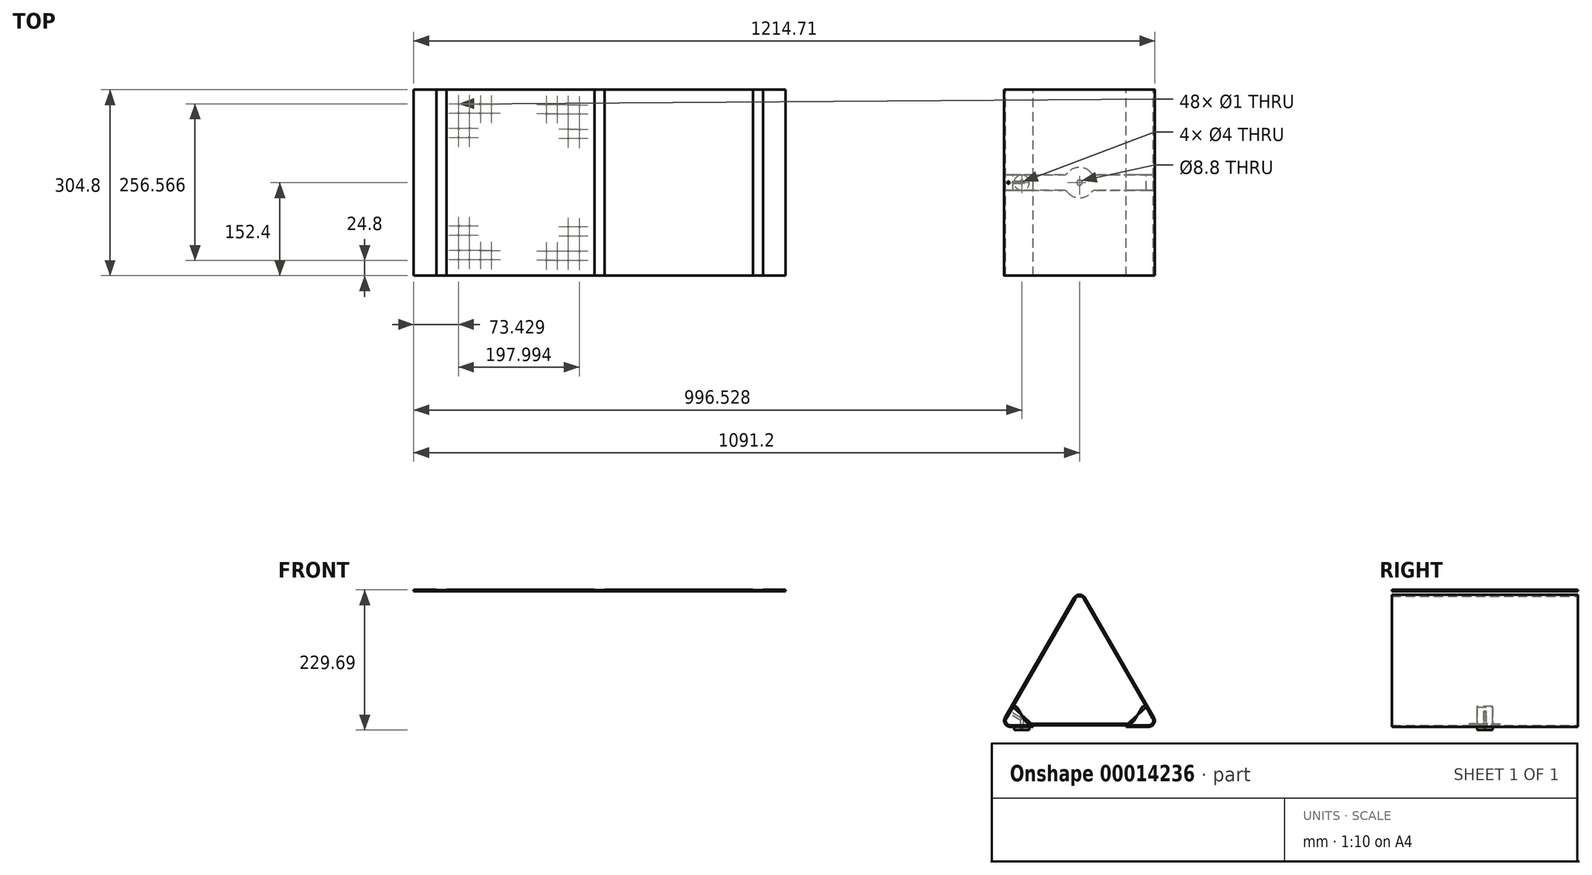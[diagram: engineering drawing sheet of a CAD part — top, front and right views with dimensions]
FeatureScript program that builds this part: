
annotation { "Feature Type Name" : "Feature", "Feature Type Description" : "" }
export const myFeature = defineFeature(function(context is Context, id is Id, definition is map)
    precondition{}
    {
        {
            var Q0;
            Q0=qCreatedBy(makeId("Front.planeOp"),FACE);
            var sketch = newSketch(context, id + "F0", { "sketchPlane" : qUnion([Q0])});
            skLineSegment(sketch, "E0", {"start": v(-6.93, -12) * mm, "end": v(-120.07, -207.97) * mm});
            skLineSegment(sketch, "E1", {"start": v(-113.14, -219.97) * mm, "end": v(-76.2, -219.97) * mm});
            skLineSegment(sketch, "E2", {"start": v(0, 0) * mm, "end": v(0, -169.94) * mm, "construction": true});
            skLineSegment(sketch, "E3.MirrorCS", {"start": v(6.93, -12) * mm, "end": v(120.07, -207.97) * mm});
            skLineSegment(sketch, "E4.MirrorCS", {"start": v(113.14, -219.97) * mm, "end": v(76.2, -219.97) * mm});
            skPoint(sketch, "E5.visualSharp", {"position": v(0, 0) * mm});
            skArc(sketch, "E5.filletArc", {"start": v(6.93, -12) * mm, "mid": v(0, -8) * mm, "end": v(-6.93, -12) * mm});
            skPoint(sketch, "E6.visualSharp", {"position": v(127, -219.97) * mm});
            skArc(sketch, "E6.filletArc", {"start": v(113.14, -219.97) * mm, "mid": v(120.07, -215.97) * mm, "end": v(120.07, -207.97) * mm});
            skPoint(sketch, "E7.visualSharp", {"position": v(-127, -219.97) * mm});
            skArc(sketch, "E7.filletArc", {"start": v(-120.07, -207.97) * mm, "mid": v(-120.07, -215.97) * mm, "end": v(-113.14, -219.97) * mm});
            skLineSegment(sketch, "E8.0", {"start": v(113.14, -222.33) * mm, "end": v(76.2, -222.33) * mm});
            skArc(sketch, "E8.1", {"start": v(113.14, -222.33) * mm, "mid": v(122.12, -217.15) * mm, "end": v(122.12, -206.79) * mm});
            skLineSegment(sketch, "E8.2", {"start": v(8.97, -10.82) * mm, "end": v(122.12, -206.79) * mm});
            skLineSegment(sketch, "E8.3", {"start": v(-113.14, -222.33) * mm, "end": v(-76.2, -222.33) * mm});
            skArc(sketch, "E8.4", {"start": v(-122.12, -206.79) * mm, "mid": v(-122.12, -217.15) * mm, "end": v(-113.14, -222.33) * mm});
            skLineSegment(sketch, "E8.5", {"start": v(-8.97, -10.82) * mm, "end": v(-122.12, -206.79) * mm});
            skArc(sketch, "E8.6", {"start": v(8.97, -10.82) * mm, "mid": v(0, -5.64) * mm, "end": v(-8.97, -10.82) * mm});
            skLineSegment(sketch, "E9", {"start": v(-76.2, -219.97) * mm, "end": v(-76.2, -222.33) * mm});
            skLineSegment(sketch, "E10", {"start": v(76.2, -219.97) * mm, "end": v(76.2, -222.33) * mm});
            skSolve(sketch);
        }
        {
            var Q0;
            Q0 = qSketchRegion(id + "F0", true);
            extrude(context, id + "F1", {"entities" : qUnion([Q0]), "depth" : 304.8 * mm});
        }
        {
            var Q0;
            Q0=qCreatedBy(makeId("Front.planeOp"),FACE);
            cPlane(context, id + "F2", {"entities" : qUnion([Q0]), "cplaneType" : CPlaneType.OFFSET, "offset" : 152.4 * mm, "width" : 150 * mm, "height" : 150 * mm});
        }
        {
            var Q0;
            Q0=qCreatedBy(id+"F2.planeOp",FACE);
            var sketch = newSketch(context, id + "F3", { "sketchPlane" : qUnion([Q0])});
            skLineSegment(sketch, "E11.0", {"start": v(-106, -183.58) * mm, "end": v(-120.07, -207.97) * mm});
            skArc(sketch, "E12.0", {"start": v(-120.07, -207.97) * mm, "mid": v(-120.07, -215.97) * mm, "end": v(-113.14, -219.97) * mm});
            skPoint(sketch, "E13.orphan", {"position": v(-6.93, -12) * mm});
            skPoint(sketch, "E14.orphan", {"position": v(6.93, -12) * mm});
            skLineSegment(sketch, "E15.0", {"start": v(0, -216.97) * mm, "end": v(-86.71, -216.97) * mm});
            skLineSegment(sketch, "E16", {"start": v(-106, -183.58) * mm, "end": v(-86.71, -216.97) * mm});
            skLineSegment(sketch, "E17", {"start": v(0, -219.97) * mm, "end": v(0, -162.05) * mm, "construction": true});
            skLineSegment(sketch, "E18.trimOffspring", {"start": v(0, -219.97) * mm, "end": v(-113.14, -219.97) * mm});
            skPoint(sketch, "E19.0.start.orphan", {"position": v(113.14, -219.97) * mm});
            skLineSegment(sketch, "E20.MirrorCS", {"start": v(0, -216.97) * mm, "end": v(86.71, -216.97) * mm});
            skLineSegment(sketch, "E21.MirrorCS", {"start": v(0, -219.97) * mm, "end": v(113.14, -219.97) * mm});
            skLineSegment(sketch, "E22.MirrorCS", {"start": v(106, -183.58) * mm, "end": v(86.71, -216.97) * mm});
            skArc(sketch, "E23.MirrorCS", {"start": v(120.07, -207.97) * mm, "mid": v(120.07, -215.97) * mm, "end": v(113.14, -219.97) * mm});
            skLineSegment(sketch, "E24.MirrorCS", {"start": v(106, -183.58) * mm, "end": v(120.07, -207.97) * mm});
            skSolve(sketch);
        }
        {
            var Q0;
            Q0 = qSketchRegion(id + "F3", true);
            extrude(context, id + "F4", {"entities" : qUnion([Q0]), "endBound" : BoundingType.SYMMETRIC, "depth" : 25 * mm});
        }
        {
            var Q0;
            Q0=makeQuery(id+"F4.opExtrude","SWEPT_EDGE",EDGE,{"disambiguationData":[OSD([sQuery(id+"F3.wireOp",EDGE,"E15.0"),sQuery(id+"F3.wireOp",EDGE,"E16")])]});
            var Q1;
            Q1=makeQuery(id+"F4.opExtrude","SWEPT_EDGE",EDGE,{"disambiguationData":[OSD([sQuery(id+"F3.wireOp",EDGE,"E20.MirrorCS"),sQuery(id+"F3.wireOp",EDGE,"E22.MirrorCS")])]});
            fillet(context, id + "F5", {"entities" : qUnion([Q0, Q1]), "radius" : 10 * mm, "tangentPropagation" : true, "allowEdgeOverflow" : false});
        }
        {
            var Q0;
            Q0=makeQuery(id+"F4.opExtrude","SWEPT_EDGE",EDGE,{"disambiguationData":[OSD([sQuery(id+"F3.wireOp",EDGE,"E22.MirrorCS"),sQuery(id+"F3.wireOp",EDGE,"E24.MirrorCS")])]});
            var Q1;
            Q1=makeQuery(id+"F4.opExtrude","SWEPT_EDGE",EDGE,{"disambiguationData":[OSD([sQuery(id+"F3.wireOp",EDGE,"E11.0"),sQuery(id+"F3.wireOp",EDGE,"E16")])]});
            fillet(context, id + "F6", {"entities" : qUnion([Q0, Q1]), "radius" : 5 * mm, "tangentPropagation" : true, "allowEdgeOverflow" : false});
        }
        {
            var Q0;
            Q0=makeQuery(id+"F4.opExtrude","SWEPT_FACE",FACE,{"disambiguationData":[OSD([sQuery(id+"F3.wireOp",EDGE,"E15.0"),sQuery(id+"F3.wireOp",EDGE,"E20.MirrorCS")])]});
            var sketch = newSketch(context, id + "F7", { "sketchPlane" : qUnion([Q0])});
            skLineSegment(sketch, "E25", {"start": v(-80.94, -152.4) * mm, "end": v(80.94, -152.4) * mm, "construction": true});
            skPoint(sketch, "E26", {"position": v(0, -152.4) * mm});
            skCircle(sketch, "E27", {"center": v(0, -152.4) * mm, "radius": 25 * mm});
            skSolve(sketch);
        }
        {
            var Q0;
            Q0 = qSketchRegion(id + "F7", true);
            var Q1;
            Q1=makeQuery(id+"F4.opExtrude","SWEPT_FACE",FACE,{"disambiguationData":[OSD([sQuery(id+"F3.wireOp",EDGE,"E18.trimOffspring"),sQuery(id+"F3.wireOp",EDGE,"E21.MirrorCS")])]});
            extrude(context, id + "F8", {"entities" : qUnion([Q0]), "operationType" : NewBodyOperationType.ADD, "endBound" : BoundingType.UP_TO_SURFACE, "oppositeDirection" : true, "endBoundEntityFace" : qUnion([Q1]), "depth" : 25 * mm});
        }
        {
            var Q0;
            Q0=makeQuery(id+"F8.boolean.opBoolean","INTERSECT",EDGE,{"disambiguationData":[OD(1.0)],"derivedFrom":[makeQuery(id+"F4.opExtrude","CAP_FACE",FACE,{"disambiguationData":[OSD([sQuery(id+"F3.wireOp",EDGE,"E11.0"),sQuery(id+"F3.wireOp",EDGE,"E12.0"),sQuery(id+"F3.wireOp",EDGE,"E15.0"),sQuery(id+"F3.wireOp",EDGE,"E16"),sQuery(id+"F3.wireOp",EDGE,"E18.trimOffspring"),sQuery(id+"F3.wireOp",EDGE,"E20.MirrorCS"),sQuery(id+"F3.wireOp",EDGE,"E21.MirrorCS"),sQuery(id+"F3.wireOp",EDGE,"E22.MirrorCS"),sQuery(id+"F3.wireOp",EDGE,"E23.MirrorCS"),sQuery(id+"F3.wireOp",EDGE,"E24.MirrorCS")])],"isStart":false}),makeQuery(id+"F8.opExtrude","SWEPT_FACE",FACE,{"disambiguationData":[OSD([sQuery(id+"F7.wireOp",EDGE,"E27")])]})]});
            var Q1;
            Q1=makeQuery(id+"F8.boolean.opBoolean","INTERSECT",EDGE,{"disambiguationData":[OD(0.0)],"derivedFrom":[makeQuery(id+"F4.opExtrude","CAP_FACE",FACE,{"disambiguationData":[OSD([sQuery(id+"F3.wireOp",EDGE,"E11.0"),sQuery(id+"F3.wireOp",EDGE,"E12.0"),sQuery(id+"F3.wireOp",EDGE,"E15.0"),sQuery(id+"F3.wireOp",EDGE,"E16"),sQuery(id+"F3.wireOp",EDGE,"E18.trimOffspring"),sQuery(id+"F3.wireOp",EDGE,"E20.MirrorCS"),sQuery(id+"F3.wireOp",EDGE,"E21.MirrorCS"),sQuery(id+"F3.wireOp",EDGE,"E22.MirrorCS"),sQuery(id+"F3.wireOp",EDGE,"E23.MirrorCS"),sQuery(id+"F3.wireOp",EDGE,"E24.MirrorCS")])],"isStart":false}),makeQuery(id+"F8.opExtrude","SWEPT_FACE",FACE,{"disambiguationData":[OSD([sQuery(id+"F7.wireOp",EDGE,"E27")])]})]});
            var Q2;
            Q2=makeQuery(id+"F8.boolean.opBoolean","INTERSECT",EDGE,{"disambiguationData":[OD(0.0)],"derivedFrom":[makeQuery(id+"F4.opExtrude","CAP_FACE",FACE,{"disambiguationData":[OSD([sQuery(id+"F3.wireOp",EDGE,"E11.0"),sQuery(id+"F3.wireOp",EDGE,"E12.0"),sQuery(id+"F3.wireOp",EDGE,"E15.0"),sQuery(id+"F3.wireOp",EDGE,"E16"),sQuery(id+"F3.wireOp",EDGE,"E18.trimOffspring"),sQuery(id+"F3.wireOp",EDGE,"E20.MirrorCS"),sQuery(id+"F3.wireOp",EDGE,"E21.MirrorCS"),sQuery(id+"F3.wireOp",EDGE,"E22.MirrorCS"),sQuery(id+"F3.wireOp",EDGE,"E23.MirrorCS"),sQuery(id+"F3.wireOp",EDGE,"E24.MirrorCS")])],"isStart":true}),makeQuery(id+"F8.opExtrude","SWEPT_FACE",FACE,{"disambiguationData":[OSD([sQuery(id+"F7.wireOp",EDGE,"E27")])]})]});
            var Q3;
            Q3=makeQuery(id+"F8.boolean.opBoolean","INTERSECT",EDGE,{"disambiguationData":[OD(1.0)],"derivedFrom":[makeQuery(id+"F4.opExtrude","CAP_FACE",FACE,{"disambiguationData":[OSD([sQuery(id+"F3.wireOp",EDGE,"E11.0"),sQuery(id+"F3.wireOp",EDGE,"E12.0"),sQuery(id+"F3.wireOp",EDGE,"E15.0"),sQuery(id+"F3.wireOp",EDGE,"E16"),sQuery(id+"F3.wireOp",EDGE,"E18.trimOffspring"),sQuery(id+"F3.wireOp",EDGE,"E20.MirrorCS"),sQuery(id+"F3.wireOp",EDGE,"E21.MirrorCS"),sQuery(id+"F3.wireOp",EDGE,"E22.MirrorCS"),sQuery(id+"F3.wireOp",EDGE,"E23.MirrorCS"),sQuery(id+"F3.wireOp",EDGE,"E24.MirrorCS")])],"isStart":true}),makeQuery(id+"F8.opExtrude","SWEPT_FACE",FACE,{"disambiguationData":[OSD([sQuery(id+"F7.wireOp",EDGE,"E27")])]})]});
            fillet(context, id + "F9", {"entities" : qUnion([Q0, Q1, Q2, Q3]), "radius" : 10 * mm, "tangentPropagation" : true, "allowEdgeOverflow" : false});
        }
        {
            var Q0;
            Q0=makeQuery(id+"F8.boolean.opBoolean","MERGE",FACE,{"derivedFrom":[makeQuery(id+"F4.opExtrude","SWEPT_FACE",FACE,{"disambiguationData":[OSD([sQuery(id+"F3.wireOp",EDGE,"E15.0"),sQuery(id+"F3.wireOp",EDGE,"E20.MirrorCS")])]}),makeQuery(id+"F8.opExtrude","CAP_FACE",FACE,{"disambiguationData":[OSD([sQuery(id+"F7.wireOp",EDGE,"E27")])],"isStart":true})]});
            var sketch = newSketch(context, id + "F10", { "sketchPlane" : qUnion([Q0])});
            skArc(sketch, "E28.0", {"start": v(19.15, -136.33) * mm, "mid": v(0, -127.4) * mm, "end": v(-19.15, -136.33) * mm, "construction": true});
            skCircle(sketch, "E29", {"center": v(0, -152.4) * mm, "radius": 4.4 * mm});
            skSolve(sketch);
        }
        {
            var Q0;
            Q0 = qSketchRegion(id + "F10", true);
            extrude(context, id + "F11", {"entities" : qUnion([Q0]), "operationType" : NewBodyOperationType.REMOVE, "oppositeDirection" : true, "depth" : 25 * mm});
        }
        {
            var Q0;
            Q0=qCreatedBy(id+"F2.planeOp",FACE);
            var sketch = newSketch(context, id + "F12", { "sketchPlane" : qUnion([Q0])});
            skLineSegment(sketch, "E30", {"start": v(-120.07, -207.97) * mm, "end": v(-6.93, -12) * mm, "construction": true});
            skArc(sketch, "E31", {"start": v(-113.14, -219.97) * mm, "mid": v(-120.07, -215.97) * mm, "end": v(-120.07, -207.97) * mm, "construction": true});
            skLineSegment(sketch, "E32", {"start": v(-76.2, -219.97) * mm, "end": v(-113.14, -219.97) * mm, "construction": true});
            skLineSegment(sketch, "E33.0", {"start": v(-119.81, -208.12) * mm, "end": v(-109.16, -189.67) * mm});
            skArc(sketch, "E33.1", {"start": v(-113.14, -219.67) * mm, "mid": v(-119.81, -215.82) * mm, "end": v(-119.81, -208.12) * mm});
            skLineSegment(sketch, "E33.2", {"start": v(-76.2, -219.67) * mm, "end": v(-113.14, -219.67) * mm});
            skLineSegment(sketch, "E34", {"start": v(0, -4.77) * mm, "end": v(0, -253.65) * mm, "construction": true});
            skLineSegment(sketch, "E35", {"start": v(-121.14, -211.97) * mm, "end": v(-121.14, -226.54) * mm, "construction": true});
            skLineSegment(sketch, "E36", {"start": v(-109.16, -189.67) * mm, "end": v(-76.2, -219.67) * mm});
            skLineSegment(sketch, "E37.MirrorCS", {"start": v(109.16, -189.67) * mm, "end": v(76.2, -219.67) * mm});
            skLineSegment(sketch, "E38.MirrorCS", {"start": v(76.2, -219.67) * mm, "end": v(113.14, -219.67) * mm});
            skLineSegment(sketch, "E39.MirrorCS", {"start": v(119.81, -208.12) * mm, "end": v(109.16, -189.67) * mm});
            skArc(sketch, "E40.MirrorCS", {"start": v(113.14, -219.67) * mm, "mid": v(119.81, -215.82) * mm, "end": v(119.81, -208.12) * mm});
            skSolve(sketch);
        }
        {
            var Q0;
            Q0 = qSketchRegion(id + "F12", true);
            extrude(context, id + "F13", {"entities" : qUnion([Q0]), "endBound" : BoundingType.SYMMETRIC, "depth" : 25 * mm});
        }
        {
            var Q0;
            Q0=makeQuery(id+"F1.opExtrude","SWEPT_FACE",FACE,{"disambiguationData":[OSD([sQuery(id+"F0.wireOp",EDGE,"E8.3")])]});
            var sketch = newSketch(context, id + "F14", { "sketchPlane" : qUnion([Q0])});
            skLineSegment(sketch, "E41.0", {"start": v(-76.2, 164.9) * mm, "end": v(-113.14, 164.9) * mm, "construction": true});
            skLineSegment(sketch, "E42.0", {"start": v(-76.2, 139.9) * mm, "end": v(-113.14, 139.9) * mm, "construction": true});
            skLineSegment(sketch, "E43", {"start": v(-94.67, 139.9) * mm, "end": v(-94.67, 164.9) * mm, "construction": true});
            skPoint(sketch, "E44", {"position": v(-94.67, 152.4) * mm});
            skCircle(sketch, "E45", {"center": v(-94.67, 152.4) * mm, "radius": 12.5 * mm});
            skCircle(sketch, "E46", {"center": v(-94.67, 152.4) * mm, "radius": 2 * mm});
            skSolve(sketch);
        }
        {
            var Q0;
            Q0 = qSketchRegion(id + "F14", true);
            extrude(context, id + "F15", {"entities" : qUnion([Q0]), "depth" : 5 * mm});
        }
        {
            var Q0;
            Q0=makeQuery(id+"F15.opExtrude","CAP_EDGE",EDGE,{"disambiguationData":[OSD([sQuery(id+"F14.wireOp",EDGE,"E46")])],"isStart":false});
            chamfer(context, id + "F16", {"entities" : qUnion([Q0]), "width" : 2 * mm, "tangentPropagation" : true});
        }
        {
            var Q0;
            Q0=makeQuery(id+"F15.opExtrude","CAP_FACE",FACE,{"disambiguationData":[OSD([sQuery(id+"F14.wireOp",EDGE,"E45"),sQuery(id+"F14.wireOp",EDGE,"E46")])],"isStart":false});
            var sketch = newSketch(context, id + "F17", { "sketchPlane" : qUnion([Q0])});
            skCircle(sketch, "E47.0", {"center": v(-94.67, 152.4) * mm, "radius": 2 * mm});
            skSolve(sketch);
        }
        {
            var Q0;
            Q0=makeQuery(id+"F17.imprint","IMPRINT",FACE,{"disambiguationData":[TD([[makeQuery(id+"F17.imprint","IMPRINT",EDGE,{"derivedFrom":sQuery(id+"F17.wireOp",EDGE,"E47.0")}),1.0]])]});
            var Q1;
            Q1=sQuery(id+"F17.wireOp",EDGE,"E47.0");
            extrude(context, id + "F18", {"entities" : qUnion([Q0]), "operationType" : NewBodyOperationType.REMOVE, "surfaceEntities" : qUnion([Q1]), "oppositeDirection" : true, "depth" : 33 * mm});
        }
        {
            var Q0;
            Q0=makeQuery(id+"F1.opExtrude","SWEPT_FACE",FACE,{"disambiguationData":[OSD([sQuery(id+"F0.wireOp",EDGE,"E8.5")])]});
            var sketch = newSketch(context, id + "F19", { "sketchPlane" : qUnion([Q0])});
            skLineSegment(sketch, "E48.0", {"start": v(139.9, -240.14) * mm, "end": v(139.9, -218.84) * mm, "construction": true});
            skLineSegment(sketch, "E49.0", {"start": v(164.9, -240.14) * mm, "end": v(164.9, -218.84) * mm, "construction": true});
            skLineSegment(sketch, "E50", {"start": v(139.9, -229.5) * mm, "end": v(164.9, -229.5) * mm, "construction": true});
            skPoint(sketch, "E51", {"position": v(152.4, -229.5) * mm});
            skCircle(sketch, "E52", {"center": v(152.4, -229.5) * mm, "radius": 2 * mm});
            skSolve(sketch);
        }
        {
            var Q0;
            Q0 = qSketchRegion(id + "F19", true);
            extrude(context, id + "F20", {"entities" : qUnion([Q0]), "operationType" : NewBodyOperationType.REMOVE, "oppositeDirection" : true, "depth" : 25 * mm});
        }
        {
            var Q0;
            Q0=qCreatedBy(makeId("Top.planeOp"),FACE);
            var sketch = newSketch(context, id + "F21", { "sketchPlane" : qUnion([Q0])});
            skLineSegment(sketch, "E53.bottom", {"start": v(-481.6, 0) * mm, "end": v(-1091.2, 0) * mm});
            skLineSegment(sketch, "E53.top", {"start": v(-481.6, -304.8) * mm, "end": v(-1091.2, -304.8) * mm});
            skLineSegment(sketch, "E53.left", {"start": v(-481.6, 0) * mm, "end": v(-481.6, -304.8) * mm});
            skLineSegment(sketch, "E53.right", {"start": v(-1091.2, 0) * mm, "end": v(-1091.2, -304.8) * mm});
            skSolve(sketch);
        }
        {
            var Q0;
            Q0 = qSketchRegion(id + "F21", true);
            extrude(context, id + "F22", {"entities" : qUnion([Q0]), "depth" : 2.36 * mm});
        }
        {
            var Q0;
            Q0=makeQuery(id+"F22.opExtrude","CAP_FACE",FACE,{"disambiguationData":[OSD([sQuery(id+"F21.wireOp",EDGE,"E53.bottom"),sQuery(id+"F21.wireOp",EDGE,"E53.top"),sQuery(id+"F21.wireOp",EDGE,"E53.left"),sQuery(id+"F21.wireOp",EDGE,"E53.right")])],"isStart":false});
            var sketch = newSketch(context, id + "F23", { "sketchPlane" : qUnion([Q0])});
            skLineSegment(sketch, "E54.right", {"start": v(-518.6, -304.8) * mm, "end": v(-518.6, 0) * mm});
            skLineSegment(sketch, "E55", {"start": v(-786.4, -304.8) * mm, "end": v(-786.4, 0) * mm, "construction": true});
            skLineSegment(sketch, "E56.bottom", {"start": v(-518.6, -304.8) * mm, "end": v(-535.35, -304.8) * mm});
            skLineSegment(sketch, "E56.top", {"start": v(-518.6, 0) * mm, "end": v(-535.35, 0) * mm});
            skLineSegment(sketch, "E56.right", {"start": v(-535.35, -304.8) * mm, "end": v(-535.35, 0) * mm});
            skLineSegment(sketch, "E57.MirrorCS", {"start": v(-1054.2, -304.8) * mm, "end": v(-1054.2, 0) * mm});
            skLineSegment(sketch, "E58.MirrorCS", {"start": v(-1037.44, -304.8) * mm, "end": v(-1037.44, 0) * mm});
            skLineSegment(sketch, "E59.MirrorCS", {"start": v(-1054.2, 0) * mm, "end": v(-1037.44, 0) * mm});
            skLineSegment(sketch, "E60.MirrorCS", {"start": v(-1054.2, -304.8) * mm, "end": v(-1037.44, -304.8) * mm});
            skLineSegment(sketch, "E61.0", {"start": v(-778.02, -304.8) * mm, "end": v(-778.02, 0) * mm});
            skLineSegment(sketch, "E62.0", {"start": v(-794.78, -304.8) * mm, "end": v(-794.78, 0) * mm});
            skLineSegment(sketch, "E63", {"start": v(-794.78, 0) * mm, "end": v(-778.02, 0) * mm});
            skLineSegment(sketch, "E64", {"start": v(-794.78, -304.8) * mm, "end": v(-778.02, -304.8) * mm});
            skSolve(sketch);
        }
        {
            var Q0;
            Q0 = qSketchRegion(id + "F23", true);
            extrude(context, id + "F24", {"entities" : qUnion([Q0]), "operationType" : NewBodyOperationType.REMOVE, "oppositeDirection" : true, "depth" : 0.25 * mm});
        }
        {
            var Q0;
            {var subQ0=sQuery(id+"F21.wireOp",EDGE,"E53.bottom");var subQ1=sQuery(id+"F21.wireOp",EDGE,"E53.top");Q0=makeQuery(id+"F24.boolean.opBoolean","SPLIT",FACE,{"disambiguationData":[TD([makeQuery(id+"F24.opExtrude","SWEPT_FACE",FACE,{"disambiguationData":[OSD([sQuery(id+"F23.wireOp",EDGE,"E58.MirrorCS")])]})])],"derivedFrom":makeQuery(id+"F22.opExtrude","CAP_FACE",FACE,{"disambiguationData":[OSD([subQ0,subQ1,sQuery(id+"F21.wireOp",EDGE,"E53.left"),sQuery(id+"F21.wireOp",EDGE,"E53.right")])],"isStart":false})});}
            var sketch = newSketch(context, id + "F25", { "sketchPlane" : qUnion([Q0])});
            skLineSegment(sketch, "E65.0.0", {"start": v(-794.78, -304.8) * mm, "end": v(-778.02, -304.8) * mm, "construction": true});
            skLineSegment(sketch, "E65.0.1", {"start": v(-778.02, -304.8) * mm, "end": v(-778.02, 0) * mm, "construction": true});
            skLineSegment(sketch, "E65.0.2", {"start": v(-778.02, 0) * mm, "end": v(-794.78, 0) * mm, "construction": true});
            skLineSegment(sketch, "E65.0.3", {"start": v(-794.78, 0) * mm, "end": v(-794.78, -304.8) * mm, "construction": true});
            skLineSegment(sketch, "E66", {"start": v(-786.4, 0) * mm, "end": v(-786.4, -304.8) * mm, "construction": true});
            skPoint(sketch, "E67", {"position": v(-819.78, -25) * mm});
            skPoint(sketch, "E68", {"position": v(-819.78, -40) * mm});
            skPoint(sketch, "E69.0.1.0", {"position": v(-819.78, -65) * mm});
            skPoint(sketch, "E69.0.1.1", {"position": v(-819.78, -80) * mm});
            skPoint(sketch, "E69.0.2.0", {"position": v(-819.78, -105) * mm});
            skPoint(sketch, "E69.0.2.1", {"position": v(-819.78, -120) * mm});
            skPoint(sketch, "E69.0.3.0", {"position": v(-819.78, -145) * mm});
            skPoint(sketch, "E69.0.3.1", {"position": v(-819.78, -160) * mm});
            skPoint(sketch, "E69.0.4.0", {"position": v(-819.78, -185) * mm});
            skPoint(sketch, "E69.0.4.1", {"position": v(-819.78, -200) * mm});
            skPoint(sketch, "E69.0.5.0", {"position": v(-819.78, -225) * mm});
            skPoint(sketch, "E69.0.5.1", {"position": v(-819.78, -240) * mm});
            skPoint(sketch, "E69.0.6.0", {"position": v(-819.78, -265) * mm});
            skPoint(sketch, "E69.0.6.1", {"position": v(-819.78, -280) * mm});
            skPoint(sketch, "E69.1.0.0", {"position": v(-837.78, -24.86) * mm});
            skPoint(sketch, "E69.1.0.1", {"position": v(-837.78, -39.86) * mm});
            skPoint(sketch, "E69.1.1.0", {"position": v(-837.78, -64.86) * mm});
            skPoint(sketch, "E69.1.1.1", {"position": v(-837.78, -79.86) * mm});
            skPoint(sketch, "E69.1.2.0", {"position": v(-837.78, -104.86) * mm});
            skPoint(sketch, "E69.1.2.1", {"position": v(-837.78, -119.86) * mm});
            skPoint(sketch, "E69.1.3.0", {"position": v(-837.78, -144.86) * mm});
            skPoint(sketch, "E69.1.3.1", {"position": v(-837.78, -159.86) * mm});
            skPoint(sketch, "E69.1.4.0", {"position": v(-837.78, -184.86) * mm});
            skPoint(sketch, "E69.1.4.1", {"position": v(-837.78, -199.86) * mm});
            skPoint(sketch, "E69.1.5.0", {"position": v(-837.78, -224.86) * mm});
            skPoint(sketch, "E69.1.5.1", {"position": v(-837.78, -239.86) * mm});
            skPoint(sketch, "E69.1.6.0", {"position": v(-837.78, -264.86) * mm});
            skPoint(sketch, "E69.1.6.1", {"position": v(-837.78, -279.86) * mm});
            skPoint(sketch, "E69.2.0.0", {"position": v(-855.78, -24.72) * mm});
            skPoint(sketch, "E69.2.0.1", {"position": v(-855.78, -39.72) * mm});
            skPoint(sketch, "E69.2.1.0", {"position": v(-855.78, -64.72) * mm});
            skPoint(sketch, "E69.2.1.1", {"position": v(-855.78, -79.72) * mm});
            skPoint(sketch, "E69.2.2.0", {"position": v(-855.78, -104.72) * mm});
            skPoint(sketch, "E69.2.2.1", {"position": v(-855.78, -119.72) * mm});
            skPoint(sketch, "E69.2.3.0", {"position": v(-855.78, -144.72) * mm});
            skPoint(sketch, "E69.2.3.1", {"position": v(-855.78, -159.72) * mm});
            skPoint(sketch, "E69.2.4.0", {"position": v(-855.78, -184.72) * mm});
            skPoint(sketch, "E69.2.4.1", {"position": v(-855.78, -199.72) * mm});
            skPoint(sketch, "E69.2.5.0", {"position": v(-855.78, -224.72) * mm});
            skPoint(sketch, "E69.2.5.1", {"position": v(-855.78, -239.72) * mm});
            skPoint(sketch, "E69.2.6.0", {"position": v(-855.78, -264.72) * mm});
            skPoint(sketch, "E69.2.6.1", {"position": v(-855.78, -279.72) * mm});
            skPoint(sketch, "E69.3.0.0", {"position": v(-873.78, -24.57) * mm});
            skPoint(sketch, "E69.3.0.1", {"position": v(-873.78, -39.57) * mm});
            skPoint(sketch, "E69.3.1.0", {"position": v(-873.78, -64.57) * mm});
            skPoint(sketch, "E69.3.1.1", {"position": v(-873.78, -79.57) * mm});
            skPoint(sketch, "E69.3.2.0", {"position": v(-873.78, -104.57) * mm});
            skPoint(sketch, "E69.3.2.1", {"position": v(-873.78, -119.57) * mm});
            skPoint(sketch, "E69.3.3.0", {"position": v(-873.78, -144.57) * mm});
            skPoint(sketch, "E69.3.3.1", {"position": v(-873.78, -159.57) * mm});
            skPoint(sketch, "E69.3.4.0", {"position": v(-873.78, -184.57) * mm});
            skPoint(sketch, "E69.3.4.1", {"position": v(-873.78, -199.57) * mm});
            skPoint(sketch, "E69.3.5.0", {"position": v(-873.78, -224.57) * mm});
            skPoint(sketch, "E69.3.5.1", {"position": v(-873.78, -239.57) * mm});
            skPoint(sketch, "E69.3.6.0", {"position": v(-873.78, -264.57) * mm});
            skPoint(sketch, "E69.3.6.1", {"position": v(-873.78, -279.57) * mm});
            skPoint(sketch, "E69.4.0.0", {"position": v(-891.78, -24.43) * mm});
            skPoint(sketch, "E69.4.0.1", {"position": v(-891.78, -39.43) * mm});
            skPoint(sketch, "E69.4.1.0", {"position": v(-891.78, -64.43) * mm});
            skPoint(sketch, "E69.4.1.1", {"position": v(-891.78, -79.43) * mm});
            skPoint(sketch, "E69.4.2.0", {"position": v(-891.78, -104.43) * mm});
            skPoint(sketch, "E69.4.2.1", {"position": v(-891.78, -119.43) * mm});
            skPoint(sketch, "E69.4.3.0", {"position": v(-891.78, -144.43) * mm});
            skPoint(sketch, "E69.4.3.1", {"position": v(-891.78, -159.43) * mm});
            skPoint(sketch, "E69.4.4.0", {"position": v(-891.78, -184.43) * mm});
            skPoint(sketch, "E69.4.4.1", {"position": v(-891.78, -199.43) * mm});
            skPoint(sketch, "E69.4.5.0", {"position": v(-891.78, -224.43) * mm});
            skPoint(sketch, "E69.4.5.1", {"position": v(-891.78, -239.43) * mm});
            skPoint(sketch, "E69.4.6.0", {"position": v(-891.78, -264.43) * mm});
            skPoint(sketch, "E69.4.6.1", {"position": v(-891.78, -279.43) * mm});
            skPoint(sketch, "E69.5.0.0", {"position": v(-909.77, -24.29) * mm});
            skPoint(sketch, "E69.5.0.1", {"position": v(-909.77, -39.29) * mm});
            skPoint(sketch, "E69.5.1.0", {"position": v(-909.77, -64.29) * mm});
            skPoint(sketch, "E69.5.1.1", {"position": v(-909.77, -79.29) * mm});
            skPoint(sketch, "E69.5.2.0", {"position": v(-909.77, -104.29) * mm});
            skPoint(sketch, "E69.5.2.1", {"position": v(-909.77, -119.29) * mm});
            skPoint(sketch, "E69.5.3.0", {"position": v(-909.77, -144.29) * mm});
            skPoint(sketch, "E69.5.3.1", {"position": v(-909.77, -159.29) * mm});
            skPoint(sketch, "E69.5.4.0", {"position": v(-909.77, -184.29) * mm});
            skPoint(sketch, "E69.5.4.1", {"position": v(-909.77, -199.29) * mm});
            skPoint(sketch, "E69.5.5.0", {"position": v(-909.77, -224.29) * mm});
            skPoint(sketch, "E69.5.5.1", {"position": v(-909.77, -239.29) * mm});
            skPoint(sketch, "E69.5.6.0", {"position": v(-909.77, -264.29) * mm});
            skPoint(sketch, "E69.5.6.1", {"position": v(-909.77, -279.29) * mm});
            skPoint(sketch, "E69.6.0.0", {"position": v(-927.77, -24.15) * mm});
            skPoint(sketch, "E69.6.0.1", {"position": v(-927.77, -39.15) * mm});
            skPoint(sketch, "E69.6.1.0", {"position": v(-927.77, -64.15) * mm});
            skPoint(sketch, "E69.6.1.1", {"position": v(-927.77, -79.15) * mm});
            skPoint(sketch, "E69.6.2.0", {"position": v(-927.77, -104.15) * mm});
            skPoint(sketch, "E69.6.2.1", {"position": v(-927.77, -119.15) * mm});
            skPoint(sketch, "E69.6.3.0", {"position": v(-927.77, -144.15) * mm});
            skPoint(sketch, "E69.6.3.1", {"position": v(-927.77, -159.15) * mm});
            skPoint(sketch, "E69.6.4.0", {"position": v(-927.77, -184.15) * mm});
            skPoint(sketch, "E69.6.4.1", {"position": v(-927.77, -199.15) * mm});
            skPoint(sketch, "E69.6.5.0", {"position": v(-927.77, -224.15) * mm});
            skPoint(sketch, "E69.6.5.1", {"position": v(-927.77, -239.15) * mm});
            skPoint(sketch, "E69.6.6.0", {"position": v(-927.77, -264.15) * mm});
            skPoint(sketch, "E69.6.6.1", {"position": v(-927.77, -279.15) * mm});
            skPoint(sketch, "E69.7.0.0", {"position": v(-945.77, -24) * mm});
            skPoint(sketch, "E69.7.0.1", {"position": v(-945.77, -39) * mm});
            skPoint(sketch, "E69.7.1.0", {"position": v(-945.77, -64) * mm});
            skPoint(sketch, "E69.7.1.1", {"position": v(-945.77, -79) * mm});
            skPoint(sketch, "E69.7.2.0", {"position": v(-945.77, -104) * mm});
            skPoint(sketch, "E69.7.2.1", {"position": v(-945.77, -119) * mm});
            skPoint(sketch, "E69.7.3.0", {"position": v(-945.77, -144) * mm});
            skPoint(sketch, "E69.7.3.1", {"position": v(-945.77, -159) * mm});
            skPoint(sketch, "E69.7.4.0", {"position": v(-945.77, -184) * mm});
            skPoint(sketch, "E69.7.4.1", {"position": v(-945.77, -199) * mm});
            skPoint(sketch, "E69.7.5.0", {"position": v(-945.77, -224) * mm});
            skPoint(sketch, "E69.7.5.1", {"position": v(-945.77, -239) * mm});
            skPoint(sketch, "E69.7.6.0", {"position": v(-945.77, -264) * mm});
            skPoint(sketch, "E69.7.6.1", {"position": v(-945.77, -279) * mm});
            skPoint(sketch, "E69.8.0.0", {"position": v(-963.77, -23.86) * mm});
            skPoint(sketch, "E69.8.0.1", {"position": v(-963.77, -38.86) * mm});
            skPoint(sketch, "E69.8.1.0", {"position": v(-963.77, -63.86) * mm});
            skPoint(sketch, "E69.8.1.1", {"position": v(-963.77, -78.86) * mm});
            skPoint(sketch, "E69.8.2.0", {"position": v(-963.77, -103.86) * mm});
            skPoint(sketch, "E69.8.2.1", {"position": v(-963.77, -118.86) * mm});
            skPoint(sketch, "E69.8.3.0", {"position": v(-963.77, -143.86) * mm});
            skPoint(sketch, "E69.8.3.1", {"position": v(-963.77, -158.86) * mm});
            skPoint(sketch, "E69.8.4.0", {"position": v(-963.77, -183.86) * mm});
            skPoint(sketch, "E69.8.4.1", {"position": v(-963.77, -198.86) * mm});
            skPoint(sketch, "E69.8.5.0", {"position": v(-963.77, -223.86) * mm});
            skPoint(sketch, "E69.8.5.1", {"position": v(-963.77, -238.86) * mm});
            skPoint(sketch, "E69.8.6.0", {"position": v(-963.77, -263.86) * mm});
            skPoint(sketch, "E69.8.6.1", {"position": v(-963.77, -278.86) * mm});
            skPoint(sketch, "E69.9.0.0", {"position": v(-981.77, -23.72) * mm});
            skPoint(sketch, "E69.9.0.1", {"position": v(-981.77, -38.72) * mm});
            skPoint(sketch, "E69.9.1.0", {"position": v(-981.77, -63.72) * mm});
            skPoint(sketch, "E69.9.1.1", {"position": v(-981.77, -78.72) * mm});
            skPoint(sketch, "E69.9.2.0", {"position": v(-981.77, -103.72) * mm});
            skPoint(sketch, "E69.9.2.1", {"position": v(-981.77, -118.72) * mm});
            skPoint(sketch, "E69.9.3.0", {"position": v(-981.77, -143.72) * mm});
            skPoint(sketch, "E69.9.3.1", {"position": v(-981.77, -158.72) * mm});
            skPoint(sketch, "E69.9.4.0", {"position": v(-981.77, -183.72) * mm});
            skPoint(sketch, "E69.9.4.1", {"position": v(-981.77, -198.72) * mm});
            skPoint(sketch, "E69.9.5.0", {"position": v(-981.77, -223.72) * mm});
            skPoint(sketch, "E69.9.5.1", {"position": v(-981.77, -238.72) * mm});
            skPoint(sketch, "E69.9.6.0", {"position": v(-981.77, -263.72) * mm});
            skPoint(sketch, "E69.9.6.1", {"position": v(-981.77, -278.72) * mm});
            skPoint(sketch, "E69.10.0.0", {"position": v(-999.77, -23.58) * mm});
            skPoint(sketch, "E69.10.0.1", {"position": v(-999.77, -38.58) * mm});
            skPoint(sketch, "E69.10.1.0", {"position": v(-999.77, -63.58) * mm});
            skPoint(sketch, "E69.10.1.1", {"position": v(-999.77, -78.58) * mm});
            skPoint(sketch, "E69.10.2.0", {"position": v(-999.77, -103.58) * mm});
            skPoint(sketch, "E69.10.2.1", {"position": v(-999.77, -118.58) * mm});
            skPoint(sketch, "E69.10.3.0", {"position": v(-999.77, -143.58) * mm});
            skPoint(sketch, "E69.10.3.1", {"position": v(-999.77, -158.58) * mm});
            skPoint(sketch, "E69.10.4.0", {"position": v(-999.77, -183.58) * mm});
            skPoint(sketch, "E69.10.4.1", {"position": v(-999.77, -198.58) * mm});
            skPoint(sketch, "E69.10.5.0", {"position": v(-999.77, -223.58) * mm});
            skPoint(sketch, "E69.10.5.1", {"position": v(-999.77, -238.58) * mm});
            skPoint(sketch, "E69.10.6.0", {"position": v(-999.77, -263.58) * mm});
            skPoint(sketch, "E69.10.6.1", {"position": v(-999.77, -278.58) * mm});
            skPoint(sketch, "E69.11.0.0", {"position": v(-1017.77, -23.43) * mm});
            skPoint(sketch, "E69.11.0.1", {"position": v(-1017.77, -38.43) * mm});
            skPoint(sketch, "E69.11.1.0", {"position": v(-1017.77, -63.43) * mm});
            skPoint(sketch, "E69.11.1.1", {"position": v(-1017.77, -78.43) * mm});
            skPoint(sketch, "E69.11.2.0", {"position": v(-1017.77, -103.43) * mm});
            skPoint(sketch, "E69.11.2.1", {"position": v(-1017.77, -118.43) * mm});
            skPoint(sketch, "E69.11.3.0", {"position": v(-1017.77, -143.43) * mm});
            skPoint(sketch, "E69.11.3.1", {"position": v(-1017.77, -158.43) * mm});
            skPoint(sketch, "E69.11.4.0", {"position": v(-1017.77, -183.43) * mm});
            skPoint(sketch, "E69.11.4.1", {"position": v(-1017.77, -198.43) * mm});
            skPoint(sketch, "E69.11.5.0", {"position": v(-1017.77, -223.43) * mm});
            skPoint(sketch, "E69.11.5.1", {"position": v(-1017.77, -238.43) * mm});
            skPoint(sketch, "E69.11.6.0", {"position": v(-1017.77, -263.43) * mm});
            skPoint(sketch, "E69.11.6.1", {"position": v(-1017.77, -278.43) * mm});
            skLineSegment(sketch, "E69.direction1", {"start": v(-819.78, -25) * mm, "end": v(-837.78, -24.86) * mm, "construction": true});
            skLineSegment(sketch, "E69.direction2", {"start": v(-819.78, -25) * mm, "end": v(-819.78, -65) * mm, "construction": true});
            skSolve(sketch);
        }
        {
            var Q0;
            Q0=sQuery(id+"F25.wireOp",VERTEX,"E69.11.0.0");
            var Q1;
            Q1=sQuery(id+"F25.wireOp",VERTEX,"E69.10.0.0");
            var Q2;
            Q2=sQuery(id+"F25.wireOp",VERTEX,"E69.10.0.1");
            var Q3;
            Q3=sQuery(id+"F25.wireOp",VERTEX,"E69.11.0.1");
            var Q4;
            Q4=sQuery(id+"F25.wireOp",VERTEX,"E69.11.1.0");
            var Q5;
            Q5=sQuery(id+"F25.wireOp",VERTEX,"E69.10.1.0");
            var Q6;
            Q6=sQuery(id+"F25.wireOp",VERTEX,"E69.10.1.1");
            var Q7;
            Q7=sQuery(id+"F25.wireOp",VERTEX,"E69.11.1.1");
            var Q8;
            Q8=sQuery(id+"F25.wireOp",VERTEX,"E67");
            var Q9;
            Q9=sQuery(id+"F25.wireOp",VERTEX,"E69.1.0.0");
            var Q10;
            Q10=sQuery(id+"F25.wireOp",VERTEX,"E69.1.0.1");
            var Q11;
            Q11=sQuery(id+"F25.wireOp",VERTEX,"E68");
            var Q12;
            Q12=sQuery(id+"F25.wireOp",VERTEX,"E69.0.1.0");
            var Q13;
            Q13=sQuery(id+"F25.wireOp",VERTEX,"E69.1.1.0");
            var Q14;
            Q14=sQuery(id+"F25.wireOp",VERTEX,"E69.1.1.1");
            var Q15;
            Q15=sQuery(id+"F25.wireOp",VERTEX,"E69.0.1.1");
            var Q16;
            Q16=sQuery(id+"F25.wireOp",VERTEX,"E69.2.0.1");
            var Q17;
            Q17=sQuery(id+"F25.wireOp",VERTEX,"E69.2.0.0");
            var Q18;
            Q18=sQuery(id+"F25.wireOp",VERTEX,"E69.3.0.0");
            var Q19;
            Q19=sQuery(id+"F25.wireOp",VERTEX,"E69.3.0.1");
            var Q20;
            Q20=sQuery(id+"F25.wireOp",VERTEX,"E69.8.0.0");
            var Q21;
            Q21=sQuery(id+"F25.wireOp",VERTEX,"E69.9.0.0");
            var Q22;
            Q22=sQuery(id+"F25.wireOp",VERTEX,"E69.9.0.1");
            var Q23;
            Q23=sQuery(id+"F25.wireOp",VERTEX,"E69.8.0.1");
            var Q24;
            Q24=sQuery(id+"F25.wireOp",VERTEX,"E69.11.6.1");
            var Q25;
            Q25=sQuery(id+"F25.wireOp",VERTEX,"E69.11.6.0");
            var Q26;
            Q26=sQuery(id+"F25.wireOp",VERTEX,"E69.11.5.1");
            var Q27;
            Q27=sQuery(id+"F25.wireOp",VERTEX,"E69.11.5.0");
            var Q28;
            Q28=sQuery(id+"F25.wireOp",VERTEX,"E69.10.5.0");
            var Q29;
            Q29=sQuery(id+"F25.wireOp",VERTEX,"E69.10.5.1");
            var Q30;
            Q30=sQuery(id+"F25.wireOp",VERTEX,"E69.10.6.0");
            var Q31;
            Q31=sQuery(id+"F25.wireOp",VERTEX,"E69.10.6.1");
            var Q32;
            Q32=sQuery(id+"F25.wireOp",VERTEX,"E69.9.6.1");
            var Q33;
            Q33=sQuery(id+"F25.wireOp",VERTEX,"E69.8.6.1");
            var Q34;
            Q34=sQuery(id+"F25.wireOp",VERTEX,"E69.8.6.0");
            var Q35;
            Q35=sQuery(id+"F25.wireOp",VERTEX,"E69.9.6.0");
            var Q36;
            Q36=sQuery(id+"F25.wireOp",VERTEX,"E69.3.6.1");
            var Q37;
            Q37=sQuery(id+"F25.wireOp",VERTEX,"E69.2.6.1");
            var Q38;
            Q38=sQuery(id+"F25.wireOp",VERTEX,"E69.1.6.1");
            var Q39;
            Q39=sQuery(id+"F25.wireOp",VERTEX,"E69.0.6.1");
            var Q40;
            Q40=sQuery(id+"F25.wireOp",VERTEX,"E69.0.6.0");
            var Q41;
            Q41=sQuery(id+"F25.wireOp",VERTEX,"E69.0.5.1");
            var Q42;
            Q42=sQuery(id+"F25.wireOp",VERTEX,"E69.0.5.0");
            var Q43;
            Q43=sQuery(id+"F25.wireOp",VERTEX,"E69.1.5.0");
            var Q44;
            Q44=sQuery(id+"F25.wireOp",VERTEX,"E69.1.5.1");
            var Q45;
            Q45=sQuery(id+"F25.wireOp",VERTEX,"E69.1.6.0");
            var Q46;
            Q46=sQuery(id+"F25.wireOp",VERTEX,"E69.2.6.0");
            var Q47;
            Q47=sQuery(id+"F25.wireOp",VERTEX,"E69.3.6.0");
            var Q48;
            Q48=makeQuery(id+"F22.opExtrude","SWEPT_BODY",BODY,{"disambiguationData":[OSD([sQuery(id+"F21.wireOp",EDGE,"E53.bottom"),sQuery(id+"F21.wireOp",EDGE,"E53.top"),sQuery(id+"F21.wireOp",EDGE,"E53.left"),sQuery(id+"F21.wireOp",EDGE,"E53.right")])]});
            hole(context, id + "F26", {"style" : HoleStyle.SIMPLE, "holeDiameter" : 1 * mm, "endStyle" : HoleEndStyle.THROUGH, "locations" : qUnion([Q0, Q1, Q2, Q3, Q4, Q5, Q6, Q7, Q8, Q9, Q10, Q11, Q12, Q13, Q14, Q15, Q16, Q17, Q18, Q19, Q20, Q21, Q22, Q23, Q24, Q25, Q26, Q27, Q28, Q29, Q30, Q31, Q32, Q33, Q34, Q35, Q36, Q37, Q38, Q39, Q40, Q41, Q42, Q43, Q44, Q45, Q46, Q47]), "scope" : qUnion([Q48])});
        }
    });
